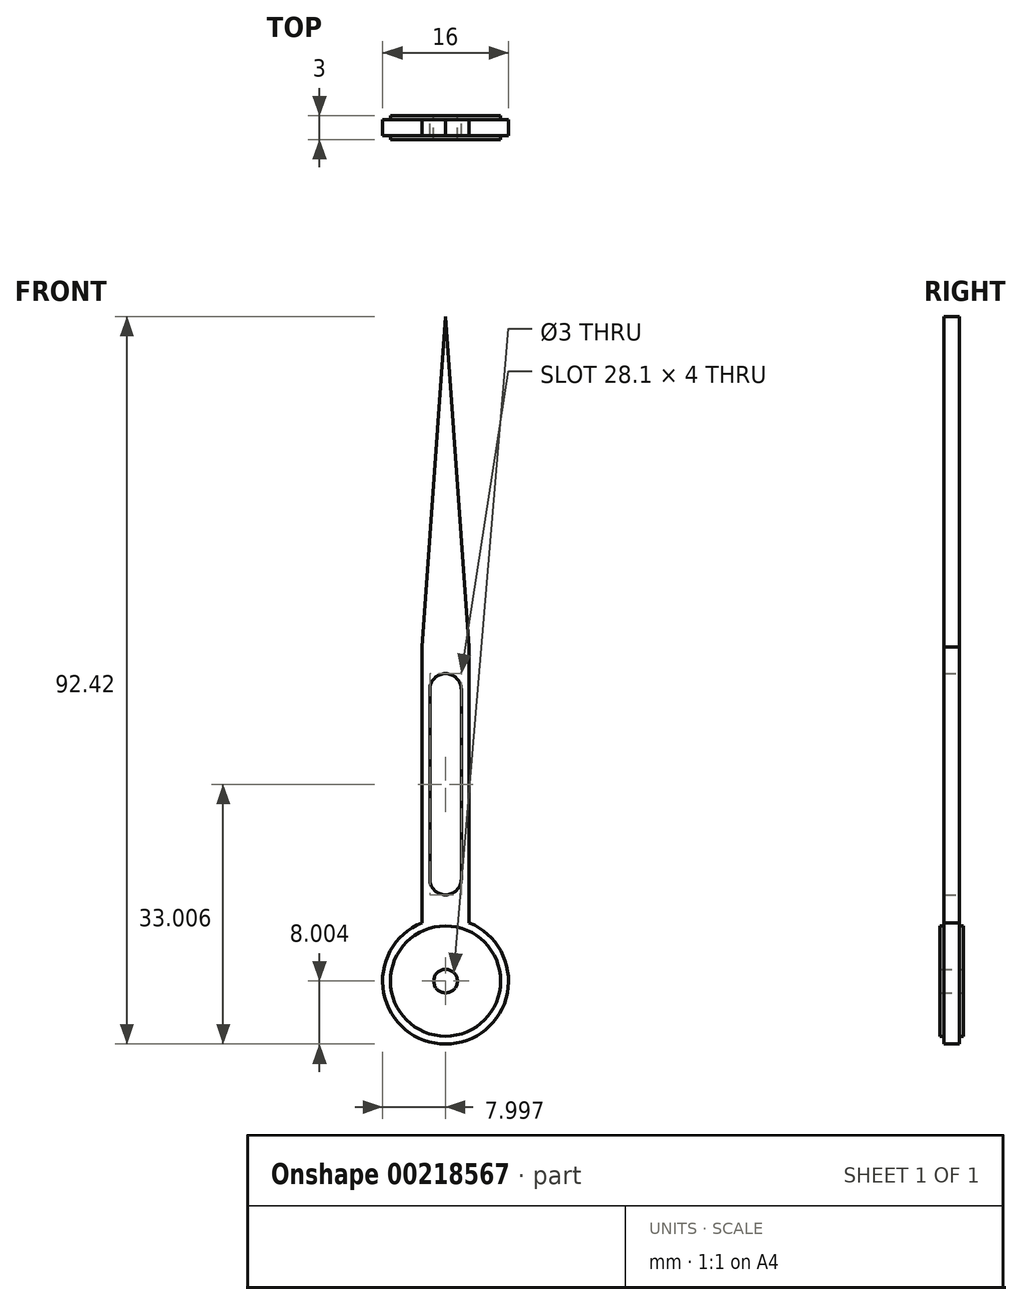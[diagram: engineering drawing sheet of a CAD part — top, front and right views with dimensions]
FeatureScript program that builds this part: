
annotation { "Feature Type Name" : "Feature", "Feature Type Description" : "" }
export const myFeature = defineFeature(function(context is Context, id is Id, definition is map)
    precondition{}
    {
        {
            var Q0;
            Q0=qCreatedBy(makeId("Front.planeOp"),FACE);
            var sketch = newSketch(context, id + "F0", { "sketchPlane" : qUnion([Q0])});
            skCircle(sketch, "E0", {"center": v(-19.83, -33.1) * mm, "radius": 1.5 * mm});
            skCircle(sketch, "E1", {"center": v(-19.83, -33.1) * mm, "radius": 7 * mm});
            skArc(sketch, "E2", {"start": v(-17.83, 3.95) * mm, "mid": v(-19.83, 5.95) * mm, "end": v(-21.83, 3.95) * mm});
            skLineSegment(sketch, "E3.MirrorCS", {"start": v(-16.83, -25.7) * mm, "end": v(-16.83, 9.3) * mm});
            skArc(sketch, "E4", {"start": v(-22.83, -25.7) * mm, "mid": v(-19.83, -41.1) * mm, "end": v(-16.83, -25.7) * mm});
            skArc(sketch, "E5", {"start": v(-21.83, -20.15) * mm, "mid": v(-19.83, -22.15) * mm, "end": v(-17.83, -20.15) * mm});
            skLineSegment(sketch, "E6", {"start": v(-21.83, 3.95) * mm, "end": v(-21.83, -20.15) * mm});
            skLineSegment(sketch, "E7", {"start": v(-17.83, -20.15) * mm, "end": v(-17.83, 3.95) * mm});
            skLineSegment(sketch, "E8.MirrorCS", {"start": v(-22.83, -25.7) * mm, "end": v(-22.83, 9.3) * mm});
            skPoint(sketch, "E9.start.orphan", {"position": v(-19.83, 9.3) * mm});
            skPoint(sketch, "E10.orphan", {"position": v(-22.83, 9.3) * mm});
            skLineSegment(sketch, "E11", {"start": v(-22.83, 9.3) * mm, "end": v(-19.83, 51.3) * mm});
            skLineSegment(sketch, "E12", {"start": v(-16.83, 9.3) * mm, "end": v(-19.83, 51.3) * mm});
            skSolve(sketch);
        }
        {
            var Q0;
            Q0=makeQuery(id+"F0.imprint","IMPRINT",FACE,{"disambiguationData":[TD([[makeQuery(id+"F0.imprint","IMPRINT",EDGE,{"derivedFrom":sQuery(id+"F0.wireOp",EDGE,"E0")}),-1.0]])]});
            var Q1;
            Q1=sQuery(id+"F0.wireOp",EDGE,"p5VHldXC-XaDy-Jo6Q-gzRM-BKwmdG1nrnMR");
            var Q2;
            Q2=sQuery(id+"F0.wireOp",EDGE,"WyDkhZpA-9s04-8oUv-ohR5-d8g4u36zodpv");
            var Q3;
            Q3=sQuery(id+"F0.wireOp",EDGE,"zPygVgP6-IXea-uzZJ-7nVa-Sz4MqIU0xlYZ");
            extrude(context, id + "F1", {"entities" : qUnion([Q0]), "surfaceEntities" : qUnion([Q1, Q2, Q3]), "depth" : 3 * mm, "symmetric" : true});
        }
        {
            var Q0;
            Q0=makeQuery(id+"F0.imprint","IMPRINT",FACE,{"disambiguationData":[TD([[makeQuery(id+"F0.imprint","IMPRINT",EDGE,{"derivedFrom":sQuery(id+"F0.wireOp",EDGE,"64VVkBTR-3lK9-xNKO-ebiv-tDq6J559YHrB.left")}),-1.0]])]});
            var Q1;
            {var subQ4=sQuery(id+"F0.wireOp",EDGE,"lu1gW57d-0Vzo-OwP6-eww9-Gga1czUeg3AM.left");Q1=makeQuery(id+"F0.imprint","IMPRINT",FACE,{"disambiguationData":[TD([[makeQuery(id+"F0.imprint","IMPRINT",EDGE,{"derivedFrom":subQ4}),-1.0]])]});}
            var Q2;
            Q2=makeQuery(id+"F0.imprint","IMPRINT",FACE,{"disambiguationData":[TD([[makeQuery(id+"F0.imprint","IMPRINT",EDGE,{"derivedFrom":sQuery(id+"F0.wireOp",EDGE,"E1")}),-1.0]])]});
            extrude(context, id + "F2", {"entities" : qUnion([Q0, Q1, Q2]), "operationType" : NewBodyOperationType.ADD, "depth" : 2 * mm, "symmetric" : true});
        }
    });
